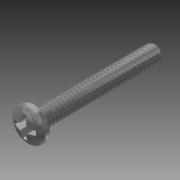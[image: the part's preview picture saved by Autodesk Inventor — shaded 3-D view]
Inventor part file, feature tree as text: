
AUTODESK INVENTOR PART (.ipt)
format: ipt  version: 2014 SP1 (Build 180222100, 222)  size: 889,856 bytes
history: native  units: in
note: dims shown in document units (in); Inventor stores cm internally (conversion verified against a paired STEP export)
features: fillet x1, other x1, imported_body x1
ambient origin geometry x8: Origin, YZ Plane, XZ Plane, XY Plane, X Axis, Y Axis, Z Axis, Center Point
bodies: Body1 (feature_tree)
feature tree (3):
  fillet  "Fillet1"  [1 undecoded]
  other  "91772A1531"
  imported_body  "Base1"
note: 1 required parameter value undecoded (feature->parameter linkage not recoverable at this tier; creation-order binding heuristic only, values carry confidence <= 0.55)
